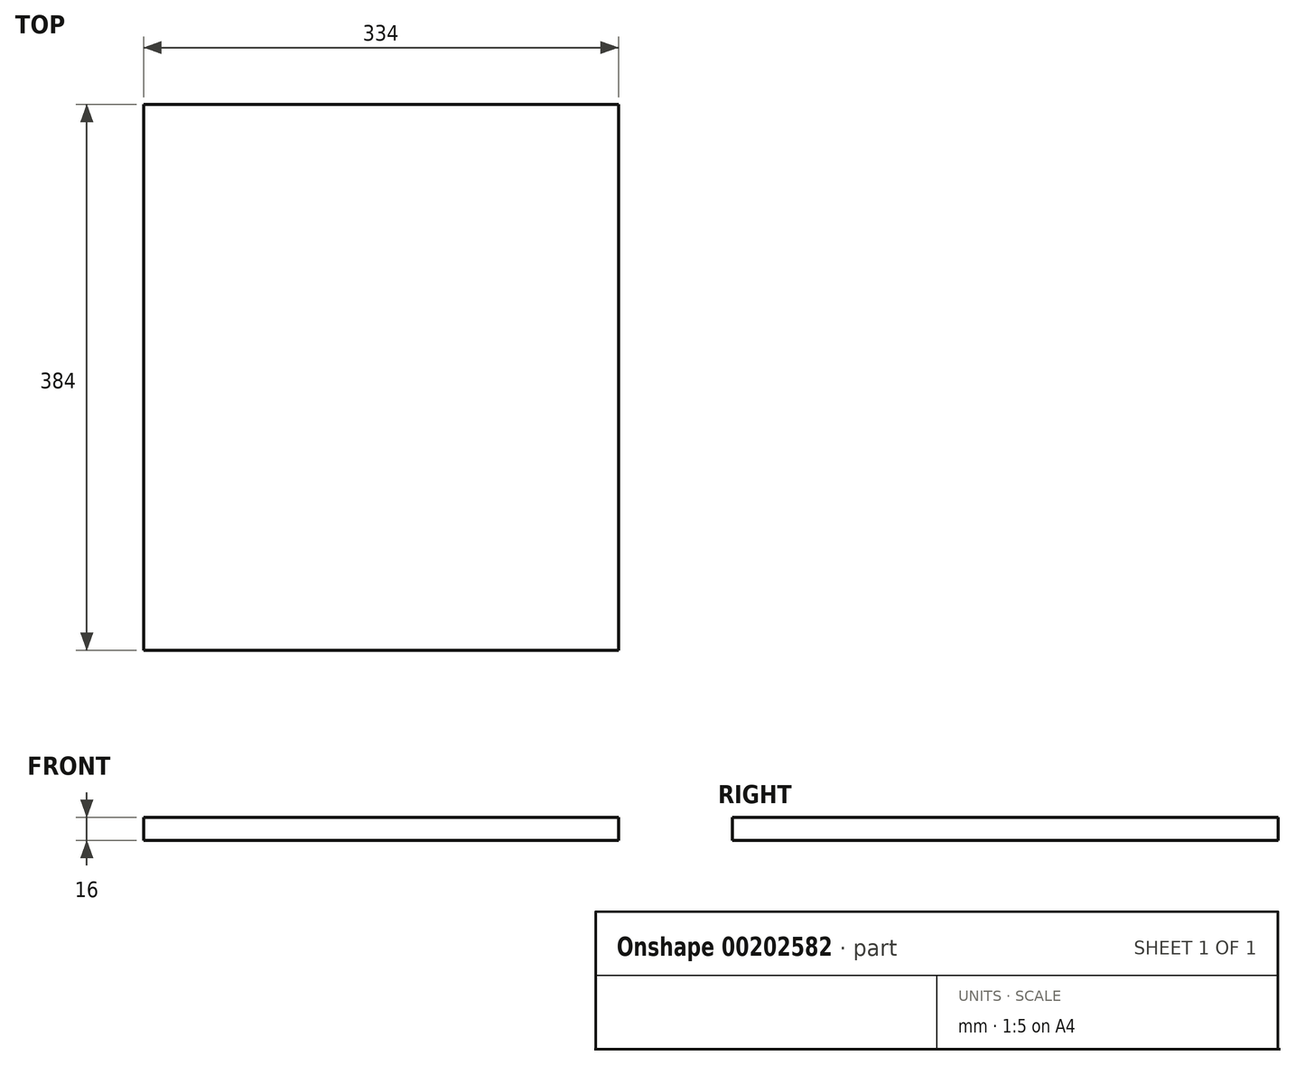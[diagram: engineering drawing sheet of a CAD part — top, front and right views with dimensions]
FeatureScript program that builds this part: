
annotation { "Feature Type Name" : "Feature", "Feature Type Description" : "" }
export const myFeature = defineFeature(function(context is Context, id is Id, definition is map)
    precondition{}
    {
        {
            var Q0;
            Q0=qCreatedBy(makeId("Top.planeOp"),FACE);
            var sketch = newSketch(context, id + "F0", { "sketchPlane" : qUnion([Q0])});
            skLineSegment(sketch, "E0.bottom", {"start": v(-864.34, -235.28) * mm, "end": v(-530.34, -235.28) * mm});
            skLineSegment(sketch, "E0.top", {"start": v(-864.34, 148.72) * mm, "end": v(-530.34, 148.72) * mm});
            skLineSegment(sketch, "E0.left", {"start": v(-864.34, -235.28) * mm, "end": v(-864.34, 148.72) * mm});
            skLineSegment(sketch, "E0.right", {"start": v(-530.34, -235.28) * mm, "end": v(-530.34, 148.72) * mm});
            skSolve(sketch);
        }
        {
            var Q0;
            Q0=makeQuery(id+"F0.imprint","IMPRINT",FACE,{"disambiguationData":[TD([[makeQuery(id+"F0.imprint","IMPRINT",EDGE,{"derivedFrom":sQuery(id+"F0.wireOp",EDGE,"E0.bottom")}),1.0]])]});
            extrude(context, id + "F1", {"entities" : qUnion([Q0]), "depth" : 16 * mm});
        }
    });
